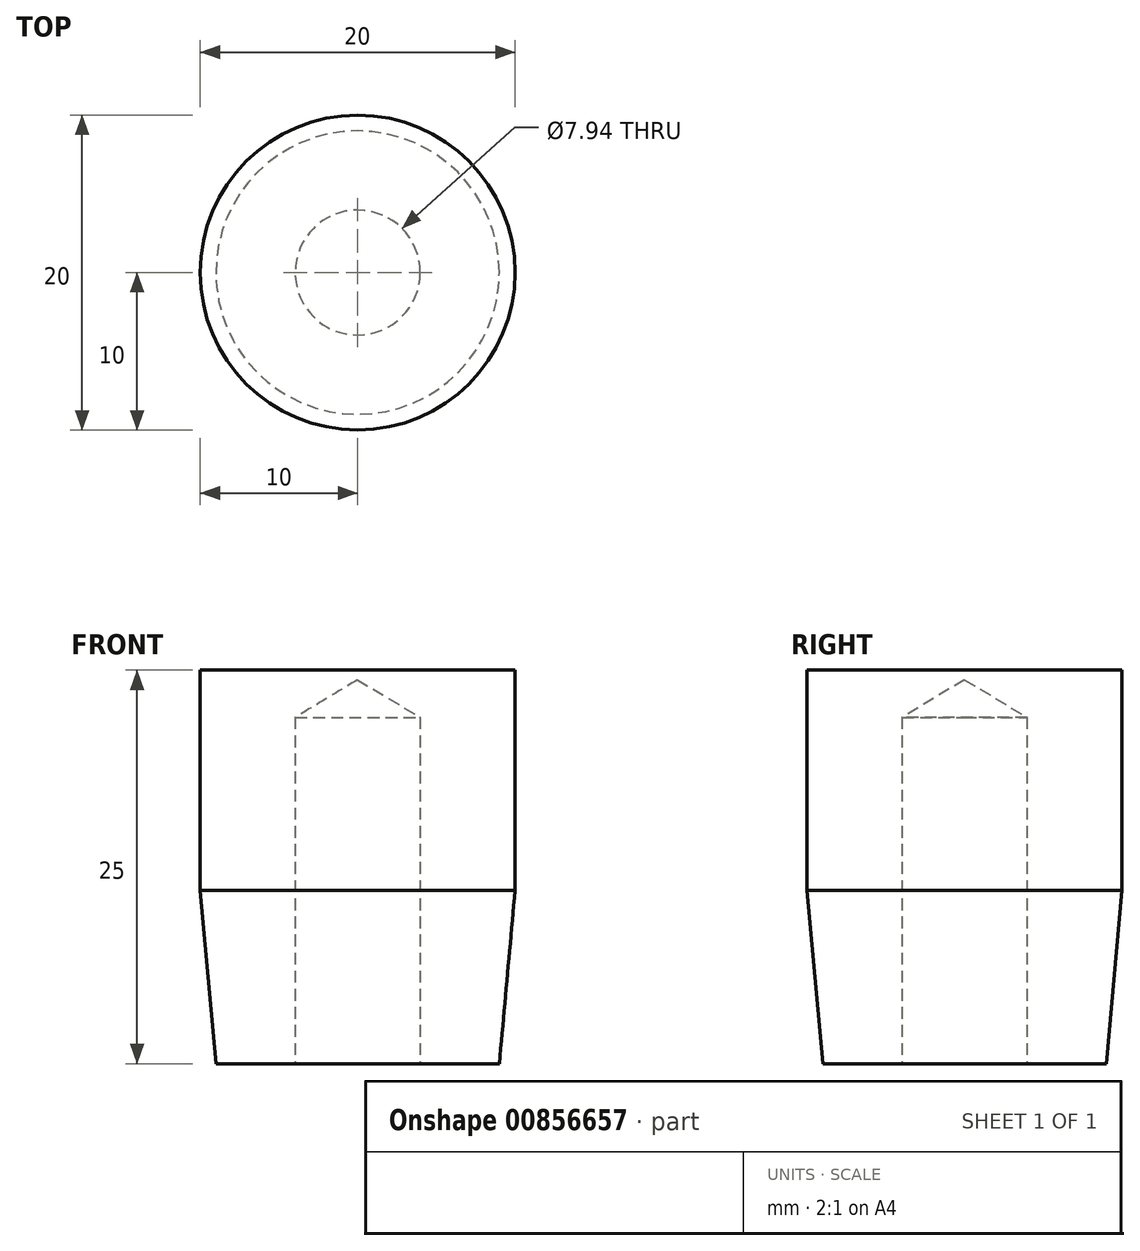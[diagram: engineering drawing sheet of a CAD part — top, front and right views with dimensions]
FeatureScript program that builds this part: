
annotation { "Feature Type Name" : "Feature", "Feature Type Description" : "" }
export const myFeature = defineFeature(function(context is Context, id is Id, definition is map)
    precondition{}
    {
        {
            var Q0;
            Q0=qCreatedBy(makeId("Top.planeOp"),FACE);
            var sketch = newSketch(context, id + "F0", { "sketchPlane" : qUnion([Q0])});
            skCircle(sketch, "E0", {"center": v(0, 0) * mm, "radius": 10 * mm});
            skSolve(sketch);
        }
        {
            var Q0;
            Q0=makeQuery(id+"F0.imprint","IMPRINT",FACE,{"disambiguationData":[TD([[makeQuery(id+"F0.imprint","IMPRINT",EDGE,{"derivedFrom":sQuery(id+"F0.wireOp",EDGE,"E0")}),1.0]])]});
            extrude(context, id + "F1", {"entities" : qUnion([Q0]), "depth" : 25 * mm, "offsetDistance" : 25 * mm});
        }
        {
            var Q0;
            Q0=sQuery(id+"F0.wireOp",VERTEX,"E0.center");
            var Q1;
            Q1=makeQuery(id+"F1.opExtrude","SWEPT_BODY",BODY,{"disambiguationData":[OSD([sQuery(id+"F0.wireOp",EDGE,"E0")])]});
            hole(context, id + "F2", {"style" : HoleStyle.SIMPLE, "endStyle" : HoleEndStyle.BLIND, "oppositeDirection" : true, "standardTappedOrClearance" : lookupTablePath({ "standard" : "ANSI", "engagement" : "75%", "pitch" : "16 tpi", "size" : "3/8", "type" : "Tapped" }), "standardBlindInLast" : lookupTablePath({ "standard" : "ANSI", "engagement" : "75%", "pitch" : "16 tpi", "size" : "3/8", "type" : "Tapped" }), "holeDiameter" : 7.94 * mm, "majorDiameter" : 9.52 * mm, "showTappedDepth" : true, "holeDepth" : 22 * mm, "isTappedThrough" : true, "tappedDepth" : 17.24 * mm, "tapClearance" : 3, "locations" : qUnion([Q0]), "scope" : qUnion([Q1])});
        }
        {
            var Q0;
            Q0=qCreatedBy(makeId("Front.planeOp"),FACE);
            var sketch = newSketch(context, id + "F3", { "sketchPlane" : qUnion([Q0])});
            skLineSegment(sketch, "E1", {"start": v(-10, 0) * mm, "end": v(-10, 11) * mm});
            skLineSegment(sketch, "E2", {"start": v(-10, 11) * mm, "end": v(-9, 0) * mm});
            skLineSegment(sketch, "E3", {"start": v(-9, 0) * mm, "end": v(-10, 0) * mm});
            skLineSegment(sketch, "E4", {"start": v(0, 0) * mm, "end": v(0, 11) * mm, "construction": true});
            skSolve(sketch);
        }
        {
            var Q0;
            Q0=qSketchRegion(id+"F3",true);
            var Q1;
            Q1=sQuery(id+"F3.wireOp",EDGE,"E4");
            revolve(context, id + "F4", {"operationType" : NewBodyOperationType.REMOVE, "surfaceOperationType" : NewSurfaceOperationType.NEW, "entities" : qUnion([Q0]), "axis" : qUnion([Q1]), "revolveType" : RevolveType.FULL, "oppositeDirection" : true});
        }
    });
